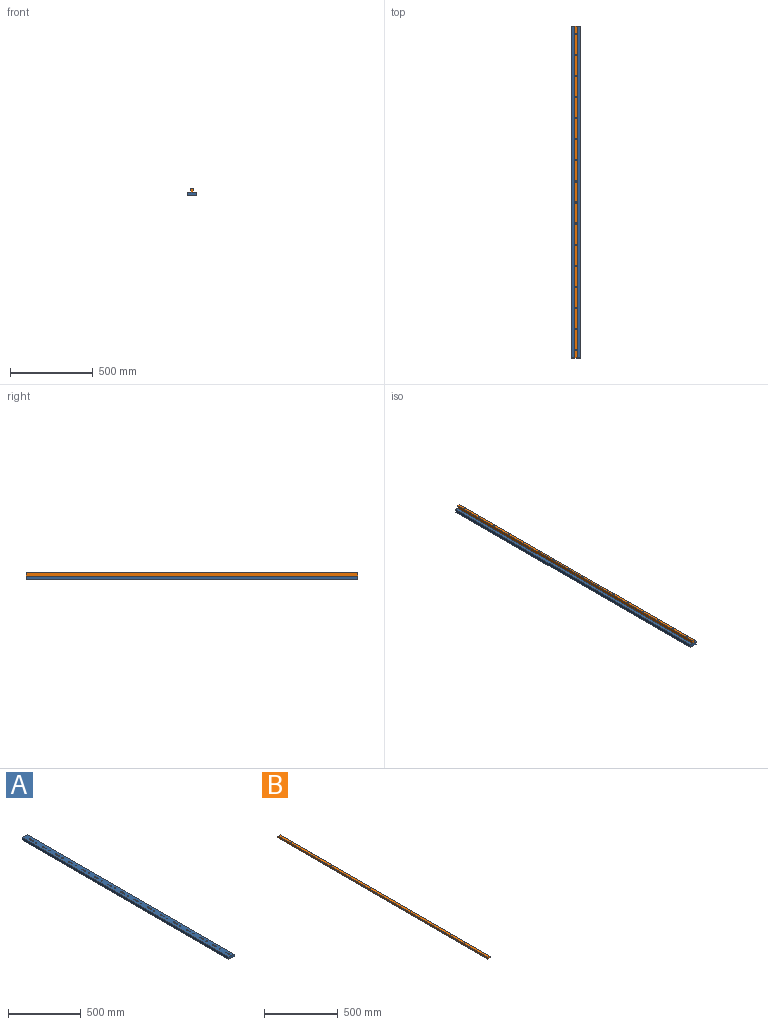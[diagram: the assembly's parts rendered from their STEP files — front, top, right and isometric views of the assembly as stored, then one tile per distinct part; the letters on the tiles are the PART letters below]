
ASSEMBLY  parts=2 mates=1
PART A: 116 faces, bbox 50x2006.4x20 mm
  f0: plane 2006.4x50mm, normal (0,0,1), area 97442.8mm2, adj f1,f3,f4,f5,f6,f9,f10,f11
  f1: plane 2006.4x20mm, normal (-1,0,0), area 40128mm2, adj f0,f2,f4,f5
  f2: plane 2006.4x50mm, normal (0,0,-1), area 96877.3mm2, adj f1,f3,f4,f5,f8,f9,f10,f13
  f3: plane 2006.4x20mm, normal (1,0,0), area 40128mm2, adj f0,f2,f4,f5
  f4: plane 50x20mm, normal (0,-1,0), area 1000mm2, adj f0,f1,f2,f3
  f5: plane 50x20mm, normal (0,1,0), area 1000mm2, adj f0,f1,f2,f3
  f6: cylinder r=4mm len=12mm, axis (0,0,-1), area 301.6mm2, adj f0,f7
  f7: plane 13x13mm, normal (0,0,-1), area 82.5mm2, adj f6,f8
  f8: cylinder r=6.5mm len=13mm, axis (0,0,-1), area 326.7mm2, adj f2,f7
  f9: cylinder r=3.2mm len=20mm, axis (0,0,-1), area 402.1mm2, adj f0,f2
  f10: cylinder r=4mm len=20mm, axis (0,0,-1), area 502.7mm2, adj f0,f2
  f11: cylinder r=4mm len=12mm, axis (0,0,-1), area 301.6mm2, adj f0,f12
  f12: plane 13x13mm, normal (0,0,-1), area 82.5mm2, adj f11,f13
  f13: cylinder r=6.5mm len=13mm, axis (0,0,-1), area 326.7mm2, adj f2,f12
  f14: cylinder r=3.2mm len=20mm, axis (0,0,-1), area 402.1mm2, adj f0,f2
  f15: cylinder r=4mm len=20mm, axis (0,0,-1), area 502.7mm2, adj f0,f2
  f16: cylinder r=4mm len=12mm, axis (0,0,-1), area 301.6mm2, adj f0,f17
  f17: plane 13x13mm, normal (0,0,-1), area 82.5mm2, adj f16,f18
  f18: cylinder r=6.5mm len=13mm, axis (0,0,-1), area 326.7mm2, adj f2,f17
  f19: cylinder r=3.2mm len=20mm, axis (0,0,-1), area 402.1mm2, adj f0,f2
  f20: cylinder r=4mm len=20mm, axis (0,0,-1), area 502.7mm2, adj f0,f2
  f21: cylinder r=4mm len=12mm, axis (0,0,-1), area 301.6mm2, adj f0,f22
  f22: plane 13x13mm, normal (0,0,-1), area 82.5mm2, adj f21,f23
  f23: cylinder r=6.5mm len=13mm, axis (0,0,-1), area 326.7mm2, adj f2,f22
  f24: cylinder r=3.2mm len=20mm, axis (0,0,-1), area 402.1mm2, adj f0,f2
  f25: cylinder r=4mm len=20mm, axis (0,0,-1), area 502.7mm2, adj f0,f2
  f26: cylinder r=4mm len=12mm, axis (0,0,-1), area 301.6mm2, adj f0,f27
  f27: plane 13x13mm, normal (0,0,-1), area 82.5mm2, adj f26,f28
  f28: cylinder r=6.5mm len=13mm, axis (0,0,-1), area 326.7mm2, adj f2,f27
  f29: cylinder r=3.2mm len=20mm, axis (0,0,-1), area 402.1mm2, adj f0,f2
  f30: cylinder r=4mm len=20mm, axis (0,0,-1), area 502.7mm2, adj f0,f2
  f31: cylinder r=4mm len=12mm, axis (0,0,-1), area 301.6mm2, adj f0,f32
  f32: plane 13x13mm, normal (0,0,-1), area 82.5mm2, adj f31,f33
  f33: cylinder r=6.5mm len=13mm, axis (0,0,-1), area 326.7mm2, adj f2,f32
  f34: cylinder r=3.2mm len=20mm, axis (0,0,-1), area 402.1mm2, adj f0,f2
  f35: cylinder r=4mm len=20mm, axis (0,0,-1), area 502.7mm2, adj f0,f2
  f36: cylinder r=4mm len=12mm, axis (0,0,-1), area 301.6mm2, adj f0,f37
  f37: plane 13x13mm, normal (0,0,-1), area 82.5mm2, adj f36,f38
  f38: cylinder r=6.5mm len=13mm, axis (0,0,-1), area 326.7mm2, adj f2,f37
  f39: cylinder r=3.2mm len=20mm, axis (0,0,-1), area 402.1mm2, adj f0,f2
  f40: cylinder r=4mm len=20mm, axis (0,0,-1), area 502.7mm2, adj f0,f2
  f41: cylinder r=4mm len=12mm, axis (0,0,-1), area 301.6mm2, adj f0,f42
  f42: plane 13x13mm, normal (0,0,-1), area 82.5mm2, adj f41,f43
  f43: cylinder r=6.5mm len=13mm, axis (0,0,-1), area 326.7mm2, adj f2,f42
  f44: cylinder r=3.2mm len=20mm, axis (0,0,-1), area 402.1mm2, adj f0,f2
  f45: cylinder r=4mm len=20mm, axis (0,0,-1), area 502.7mm2, adj f0,f2
  f46: cylinder r=4mm len=12mm, axis (0,0,-1), area 301.6mm2, adj f0,f47
  f47: plane 13x13mm, normal (0,0,-1), area 82.5mm2, adj f46,f48
  f48: cylinder r=6.5mm len=13mm, axis (0,0,-1), area 326.7mm2, adj f2,f47
  f49: cylinder r=3.2mm len=20mm, axis (0,0,-1), area 402.1mm2, adj f0,f2
  f50: cylinder r=4mm len=20mm, axis (0,0,-1), area 502.7mm2, adj f0,f2
  f51: cylinder r=4mm len=12mm, axis (0,0,-1), area 301.6mm2, adj f0,f52
  f52: plane 13x13mm, normal (0,0,-1), area 82.5mm2, adj f51,f53
  f53: cylinder r=6.5mm len=13mm, axis (0,0,-1), area 326.7mm2, adj f2,f52
  f54: cylinder r=3.2mm len=20mm, axis (0,0,-1), area 402.1mm2, adj f0,f2
  f55: cylinder r=4mm len=20mm, axis (0,0,-1), area 502.7mm2, adj f0,f2
  f56: cylinder r=4mm len=12mm, axis (0,0,-1), area 301.6mm2, adj f0,f57
  f57: plane 13x13mm, normal (0,0,-1), area 82.5mm2, adj f56,f58
  f58: cylinder r=6.5mm len=13mm, axis (0,0,-1), area 326.7mm2, adj f2,f57
  f59: cylinder r=3.2mm len=20mm, axis (0,0,-1), area 402.1mm2, adj f0,f2
  f60: cylinder r=4mm len=20mm, axis (0,0,-1), area 502.7mm2, adj f0,f2
  f61: cylinder r=4mm len=12mm, axis (0,0,-1), area 301.6mm2, adj f0,f62
  f62: plane 13x13mm, normal (0,0,-1), area 82.5mm2, adj f61,f63
  f63: cylinder r=6.5mm len=13mm, axis (0,0,-1), area 326.7mm2, adj f2,f62
  f64: cylinder r=3.2mm len=20mm, axis (0,0,-1), area 402.1mm2, adj f0,f2
  f65: cylinder r=4mm len=20mm, axis (0,0,-1), area 502.7mm2, adj f0,f2
  f66: cylinder r=4mm len=12mm, axis (0,0,-1), area 301.6mm2, adj f0,f67
  f67: plane 13x13mm, normal (0,0,-1), area 82.5mm2, adj f66,f68
  f68: cylinder r=6.5mm len=13mm, axis (0,0,-1), area 326.7mm2, adj f2,f67
  f69: cylinder r=3.2mm len=20mm, axis (0,0,-1), area 402.1mm2, adj f0,f2
  f70: cylinder r=4mm len=20mm, axis (0,0,-1), area 502.7mm2, adj f0,f2
  f71: cylinder r=4mm len=12mm, axis (0,0,-1), area 301.6mm2, adj f0,f72
  f72: plane 13x13mm, normal (0,0,-1), area 82.5mm2, adj f71,f73
  f73: cylinder r=6.5mm len=13mm, axis (0,0,-1), area 326.7mm2, adj f2,f72
  f74: cylinder r=3.2mm len=20mm, axis (0,0,-1), area 402.1mm2, adj f0,f2
  f75: cylinder r=4mm len=20mm, axis (0,0,-1), area 502.7mm2, adj f0,f2
  f76: cylinder r=4mm len=12mm, axis (0,0,-1), area 301.6mm2, adj f0,f77
  f77: plane 13x13mm, normal (0,0,-1), area 82.5mm2, adj f76,f78
  f78: cylinder r=6.5mm len=13mm, axis (0,0,-1), area 326.7mm2, adj f2,f77
  f79: cylinder r=3.2mm len=20mm, axis (0,0,-1), area 402.1mm2, adj f0,f2
  f80: cylinder r=4mm len=20mm, axis (0,0,-1), area 502.7mm2, adj f0,f2
  f81: cylinder r=4mm len=12mm, axis (0,0,-1), area 301.6mm2, adj f0,f82
  f82: plane 13x13mm, normal (0,0,-1), area 82.5mm2, adj f81,f83
  f83: cylinder r=6.5mm len=13mm, axis (0,0,-1), area 326.7mm2, adj f2,f82
  f84: cylinder r=3.2mm len=20mm, axis (0,0,-1), area 402.1mm2, adj f0,f2
  f85: cylinder r=4mm len=20mm, axis (0,0,-1), area 502.7mm2, adj f0,f2
  f86: cylinder r=4mm len=10mm, axis (0,0,1), area 251.3mm2, adj f0,f87
  f87: cone r=0mm half-angle=59deg, axis (0,0,1), area 58.6mm2, adj f86
  f88: cylinder r=4mm len=10mm, axis (0,0,1), area 251.3mm2, adj f0,f89
  f89: cone r=0mm half-angle=59deg, axis (0,0,1), area 58.6mm2, adj f88
  f90: cylinder r=4mm len=10mm, axis (0,0,1), area 251.3mm2, adj f0,f91
  f91: cone r=0mm half-angle=59deg, axis (0,0,1), area 58.6mm2, adj f90
  f92: cylinder r=4mm len=10mm, axis (0,0,1), area 251.3mm2, adj f0,f93
  f93: cone r=0mm half-angle=59deg, axis (0,0,1), area 58.6mm2, adj f92
  f94: cylinder r=4mm len=10mm, axis (0,0,1), area 251.3mm2, adj f0,f95
  f95: cone r=0mm half-angle=59deg, axis (0,0,1), area 58.6mm2, adj f94
  f96: cylinder r=4mm len=10mm, axis (0,0,1), area 251.3mm2, adj f0,f97
  f97: cone r=0mm half-angle=59deg, axis (0,0,1), area 58.6mm2, adj f96
  f98: cylinder r=4mm len=10mm, axis (0,0,1), area 251.3mm2, adj f0,f99
  f99: cone r=0mm half-angle=59deg, axis (0,0,1), area 58.6mm2, adj f98
  f100: cylinder r=4mm len=10mm, axis (0,0,1), area 251.3mm2, adj f0,f101
  f101: cone r=0mm half-angle=59deg, axis (0,0,1), area 58.6mm2, adj f100
  f102: cylinder r=4mm len=10mm, axis (0,0,1), area 251.3mm2, adj f0,f103
  f103: cone r=0mm half-angle=59deg, axis (0,0,1), area 58.6mm2, adj f102
  f104: cylinder r=4mm len=10mm, axis (0,0,1), area 251.3mm2, adj f0,f105
  f105: cone r=0mm half-angle=59deg, axis (0,0,1), area 58.6mm2, adj f104
  f106: cylinder r=4mm len=10mm, axis (0,0,1), area 251.3mm2, adj f0,f107
  f107: cone r=0mm half-angle=59deg, axis (0,0,1), area 58.6mm2, adj f106
  f108: cylinder r=4mm len=10mm, axis (0,0,1), area 251.3mm2, adj f0,f109
  f109: cone r=0mm half-angle=59deg, axis (0,0,1), area 58.6mm2, adj f108
  f110: cylinder r=4mm len=10mm, axis (0,0,1), area 251.3mm2, adj f0,f111
  f111: cone r=0mm half-angle=59deg, axis (0,0,1), area 58.6mm2, adj f110
  f112: cylinder r=4mm len=10mm, axis (0,0,1), area 251.3mm2, adj f0,f113
  f113: cone r=0mm half-angle=59deg, axis (0,0,1), area 58.6mm2, adj f112
  f114: cylinder r=4mm len=10mm, axis (0,0,1), area 251.3mm2, adj f0,f115
  f115: cone r=0mm half-angle=59deg, axis (0,0,1), area 58.6mm2, adj f114
PART B: 52 faces, bbox 20x2006.4x15 mm
  f0: plane 2006.4x20mm, normal (0,0,1), area 40128mm2, adj f1,f3,f4,f5
  f1: plane 2006.4x15mm, normal (-1,0,0), area 29581.3mm2, adj f0,f2,f4,f5,f6,f9,f12,f15
  f2: plane 2006.4x20mm, normal (0,0,-1), area 40128mm2, adj f1,f3,f4,f5
  f3: plane 2006.4x15mm, normal (1,0,0), area 28827.3mm2, adj f0,f2,f4,f5,f6,f7,f9,f10
  f4: plane 20x15mm, normal (0,-1,0), area 300mm2, adj f0,f1,f2,f3
  f5: plane 20x15mm, normal (0,1,0), area 300mm2, adj f0,f1,f2,f3
  f6: cylinder r=3.2mm len=20mm, axis (1,0,0), area 402.1mm2, adj f1,f3
  f7: cylinder r=4mm len=10mm, axis (1,0,0), area 251.3mm2, adj f3,f8
  f8: cone r=0mm half-angle=59deg, axis (1,0,0), area 58.6mm2, adj f7
  f9: cylinder r=3.2mm len=20mm, axis (1,0,0), area 402.1mm2, adj f1,f3
  f10: cylinder r=4mm len=10mm, axis (1,0,0), area 251.3mm2, adj f3,f11
  f11: cone r=0mm half-angle=59deg, axis (1,0,0), area 58.6mm2, adj f10
  f12: cylinder r=3.2mm len=20mm, axis (1,0,0), area 402.1mm2, adj f1,f3
  f13: cylinder r=4mm len=10mm, axis (1,0,0), area 251.3mm2, adj f3,f14
  f14: cone r=0mm half-angle=59deg, axis (1,0,0), area 58.6mm2, adj f13
  f15: cylinder r=3.2mm len=20mm, axis (1,0,0), area 402.1mm2, adj f1,f3
  f16: cylinder r=4mm len=10mm, axis (1,0,0), area 251.3mm2, adj f3,f17
  f17: cone r=0mm half-angle=59deg, axis (1,0,0), area 58.6mm2, adj f16
  f18: cylinder r=3.2mm len=20mm, axis (1,0,0), area 402.1mm2, adj f1,f3
  f19: cylinder r=4mm len=10mm, axis (1,0,0), area 251.3mm2, adj f3,f20
  f20: cone r=0mm half-angle=59deg, axis (1,0,0), area 58.6mm2, adj f19
  f21: cylinder r=3.2mm len=20mm, axis (1,0,0), area 402.1mm2, adj f1,f3
  f22: cylinder r=4mm len=10mm, axis (1,0,0), area 251.3mm2, adj f3,f23
  f23: cone r=0mm half-angle=59deg, axis (1,0,0), area 58.6mm2, adj f22
  f24: cylinder r=3.2mm len=20mm, axis (1,0,0), area 402.1mm2, adj f1,f3
  f25: cylinder r=4mm len=10mm, axis (1,0,0), area 251.3mm2, adj f3,f26
  f26: cone r=0mm half-angle=59deg, axis (1,0,0), area 58.6mm2, adj f25
  f27: cylinder r=3.2mm len=20mm, axis (1,0,0), area 402.1mm2, adj f1,f3
  f28: cylinder r=4mm len=10mm, axis (1,0,0), area 251.3mm2, adj f3,f29
  f29: cone r=0mm half-angle=59deg, axis (1,0,0), area 58.6mm2, adj f28
  f30: cylinder r=3.2mm len=20mm, axis (1,0,0), area 402.1mm2, adj f1,f3
  f31: cylinder r=4mm len=10mm, axis (1,0,0), area 251.3mm2, adj f3,f32
  f32: cone r=0mm half-angle=59deg, axis (1,0,0), area 58.6mm2, adj f31
  f33: cylinder r=3.2mm len=20mm, axis (1,0,0), area 402.1mm2, adj f1,f3
  f34: cylinder r=4mm len=10mm, axis (1,0,0), area 251.3mm2, adj f3,f35
  f35: cone r=0mm half-angle=59deg, axis (1,0,0), area 58.6mm2, adj f34
  f36: cylinder r=3.2mm len=20mm, axis (1,0,0), area 402.1mm2, adj f1,f3
  f37: cylinder r=4mm len=10mm, axis (1,0,0), area 251.3mm2, adj f3,f38
  f38: cone r=0mm half-angle=59deg, axis (1,0,0), area 58.6mm2, adj f37
  f39: cylinder r=3.2mm len=20mm, axis (1,0,0), area 402.1mm2, adj f1,f3
  f40: cylinder r=4mm len=10mm, axis (1,0,0), area 251.3mm2, adj f3,f41
  f41: cone r=0mm half-angle=59deg, axis (1,0,0), area 58.6mm2, adj f40
  f42: cylinder r=3.2mm len=20mm, axis (1,0,0), area 402.1mm2, adj f1,f3
  f43: cylinder r=4mm len=10mm, axis (1,0,0), area 251.3mm2, adj f3,f44
  f44: cone r=0mm half-angle=59deg, axis (1,0,0), area 58.6mm2, adj f43
  f45: cylinder r=3.2mm len=20mm, axis (1,0,0), area 402.1mm2, adj f1,f3
  f46: cylinder r=4mm len=10mm, axis (1,0,0), area 251.3mm2, adj f3,f47
  f47: cone r=0mm half-angle=59deg, axis (1,0,0), area 58.6mm2, adj f46
  f48: cylinder r=3.2mm len=20mm, axis (1,0,0), area 402.1mm2, adj f1,f3
  f49: cylinder r=4mm len=10mm, axis (1,0,0), area 251.3mm2, adj f3,f50
  f50: cone r=0mm half-angle=59deg, axis (1,0,0), area 58.6mm2, adj f49
  f51: cylinder r=3.2mm len=20mm, axis (1,0,0), area 402.1mm2, adj f1,f3
PLACE A t=(0,0,78)mm
PLACE B rot(axis=(0,1,0),90deg) t=(17.5,0,118)mm
MATE fastened B.f3 <-> A.f0  axis (0,0,-1) through (25,-2006.4,98)mm
